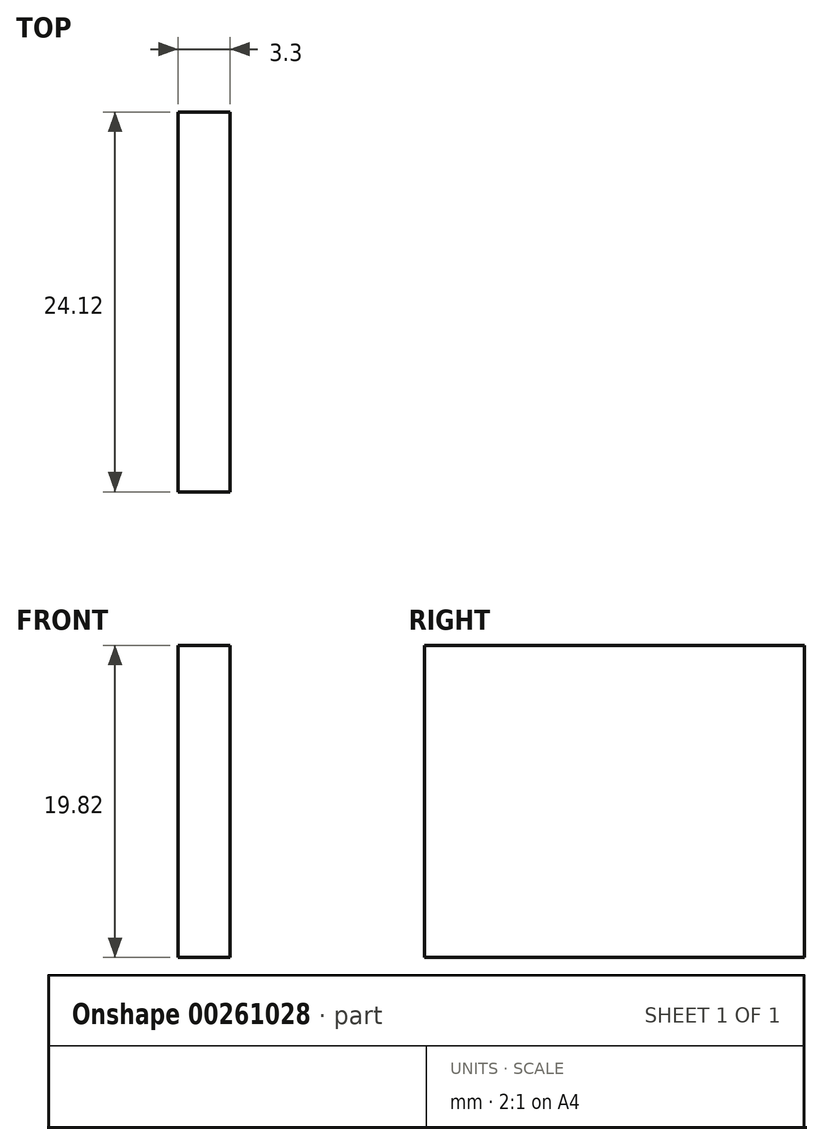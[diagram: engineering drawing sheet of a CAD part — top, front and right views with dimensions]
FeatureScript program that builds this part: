
annotation { "Feature Type Name" : "Feature", "Feature Type Description" : "" }
export const myFeature = defineFeature(function(context is Context, id is Id, definition is map)
    precondition{}
    {
        {
            var Q0;
            Q0=qCreatedBy(makeId("Right.planeOp"),FACE);
            var sketch = newSketch(context, id + "F0", { "sketchPlane" : qUnion([Q0])});
            skLineSegment(sketch, "E0.bottom", {"start": v(12.06, 9.9) * mm, "end": v(-12.07, 9.9) * mm});
            skLineSegment(sketch, "E0.top", {"start": v(12.07, -9.9) * mm, "end": v(-12.06, -9.9) * mm});
            skLineSegment(sketch, "E0.left", {"start": v(12.06, 9.9) * mm, "end": v(12.07, -9.9) * mm});
            skLineSegment(sketch, "E0.right", {"start": v(-12.07, 9.9) * mm, "end": v(-12.06, -9.9) * mm});
            skPoint(sketch, "E0.middle", {"position": v(0, 0) * mm});
            skSolve(sketch);
        }
        {
            var Q0;
            Q0=makeQuery(id+"F0.imprint","IMPRINT",FACE,{"disambiguationData":[TD([[makeQuery(id+"F0.imprint","IMPRINT",EDGE,{"derivedFrom":sQuery(id+"F0.wireOp",EDGE,"E0.bottom")}),1.0]])]});
            extrude(context, id + "F1", {"entities" : qUnion([Q0]), "depth" : 3.3 * mm});
        }
    });
